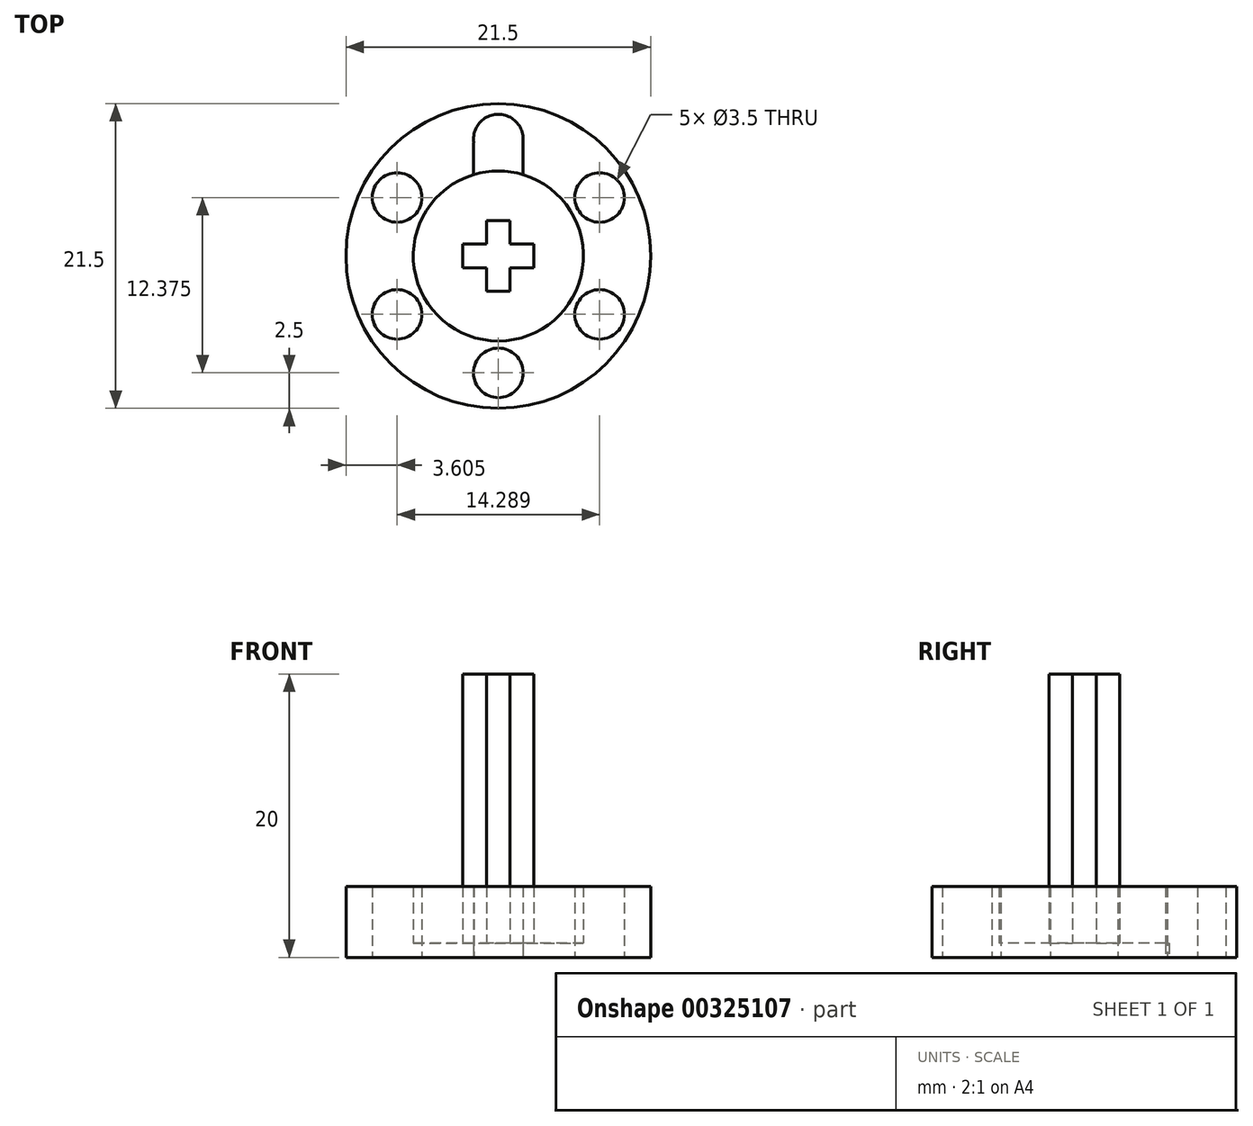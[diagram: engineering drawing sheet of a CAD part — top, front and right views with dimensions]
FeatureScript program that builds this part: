
annotation { "Feature Type Name" : "Feature", "Feature Type Description" : "" }
export const myFeature = defineFeature(function(context is Context, id is Id, definition is map)
    precondition{}
    {
        {
            var Q0;
            Q0=qCreatedBy(makeId("Top.planeOp"),FACE);
            var sketch = newSketch(context, id + "F0", { "sketchPlane" : qUnion([Q0])});
            skLineSegment(sketch, "E0", {"start": v(-0.83, 2.5) * mm, "end": v(0.83, 2.5) * mm});
            skLineSegment(sketch, "E1", {"start": v(0.83, -2.5) * mm, "end": v(-0.83, -2.5) * mm});
            skLineSegment(sketch, "E2.left", {"start": v(-2.5, 0.83) * mm, "end": v(-2.5, -0.83) * mm});
            skLineSegment(sketch, "E2.right", {"start": v(2.5, 0.83) * mm, "end": v(2.5, -0.83) * mm});
            skPoint(sketch, "E3", {"position": v(-0.83, 0.83) * mm});
            skPoint(sketch, "E4", {"position": v(0.83, 0.83) * mm});
            skPoint(sketch, "E5", {"position": v(0.83, -0.83) * mm});
            skPoint(sketch, "E6", {"position": v(-0.83, -0.83) * mm});
            skLineSegment(sketch, "E7", {"start": v(-0.83, -2.5) * mm, "end": v(-0.83, -0.83) * mm});
            skLineSegment(sketch, "E8", {"start": v(-0.83, -0.83) * mm, "end": v(-0.83, 0.83) * mm});
            skLineSegment(sketch, "E9", {"start": v(-0.83, 0.83) * mm, "end": v(-0.83, 2.5) * mm});
            skLineSegment(sketch, "E10", {"start": v(-2.5, -0.83) * mm, "end": v(-0.83, -0.83) * mm});
            skLineSegment(sketch, "E11", {"start": v(0.83, -0.83) * mm, "end": v(2.5, -0.83) * mm});
            skLineSegment(sketch, "E12", {"start": v(-0.83, -0.83) * mm, "end": v(0.83, -0.83) * mm});
            skLineSegment(sketch, "E13", {"start": v(-2.5, 0.83) * mm, "end": v(-0.83, 0.83) * mm});
            skLineSegment(sketch, "E14", {"start": v(-0.83, 0.83) * mm, "end": v(0.83, 0.83) * mm});
            skLineSegment(sketch, "E15", {"start": v(2.5, 0.83) * mm, "end": v(0.83, 0.83) * mm});
            skLineSegment(sketch, "E16", {"start": v(0.83, 2.5) * mm, "end": v(0.83, 0.83) * mm});
            skLineSegment(sketch, "E17", {"start": v(0.83, -0.83) * mm, "end": v(0.83, 0.83) * mm});
            skLineSegment(sketch, "E18", {"start": v(0.83, -2.5) * mm, "end": v(0.83, -0.83) * mm});
            skPoint(sketch, "E19", {"position": v(0, 0) * mm});
            skLineSegment(sketch, "E20", {"start": v(-0.83, -0.83) * mm, "end": v(0.83, 0.83) * mm, "construction": true});
            skLineSegment(sketch, "E21", {"start": v(-0.83, 0.83) * mm, "end": v(0.83, -0.83) * mm, "construction": true});
            skSolve(sketch);
        }
        {
            var Q0;
            Q0=qCreatedBy(makeId("Top.planeOp"),FACE);
            var sketch = newSketch(context, id + "F1", { "sketchPlane" : qUnion([Q0])});
            skCircle(sketch, "E22", {"center": v(0, 0) * mm, "radius": 6 * mm});
            skLineSegment(sketch, "E23", {"start": v(-1.75, 5.74) * mm, "end": v(-1.75, 8) * mm});
            skLineSegment(sketch, "E24", {"start": v(-1.75, 8) * mm, "end": v(1.75, 8) * mm});
            skLineSegment(sketch, "E25", {"start": v(1.75, 8) * mm, "end": v(1.75, 5.74) * mm});
            skPoint(sketch, "E26", {"position": v(0, 8) * mm});
            skCircle(sketch, "E27", {"center": v(0, 0) * mm, "radius": 10.75 * mm});
            skCircle(sketch, "E28", {"center": v(0, 0) * mm, "radius": 10 * mm});
            skCircle(sketch, "E29", {"center": v(0, -8.25) * mm, "radius": 1.75 * mm});
            skPoint(sketch, "E30", {"position": v(0, -10) * mm});
            skCircle(sketch, "E31.1.0", {"center": v(7.14, -4.13) * mm, "radius": 1.75 * mm});
            skCircle(sketch, "E31.2.0", {"center": v(7.14, 4.12) * mm, "radius": 1.75 * mm});
            skCircle(sketch, "E31.3.0", {"center": v(0, 8.25) * mm, "radius": 1.75 * mm});
            skCircle(sketch, "E31.4.0", {"center": v(-7.14, 4.13) * mm, "radius": 1.75 * mm});
            skCircle(sketch, "E31.5.0", {"center": v(-7.14, -4.13) * mm, "radius": 1.75 * mm});
            skSolve(sketch);
        }
        {
            var Q0;
            Q0=makeQuery(id+"F0.imprint","IMPRINT",FACE,{"disambiguationData":[TD([[makeQuery(id+"F0.imprint","IMPRINT",EDGE,{"derivedFrom":sQuery(id+"F0.wireOp",EDGE,"E0")}),-1.0]])]});
            var Q1;
            Q1=makeQuery(id+"F0.imprint","IMPRINT",FACE,{"disambiguationData":[TD([[makeQuery(id+"F0.imprint","IMPRINT",EDGE,{"derivedFrom":sQuery(id+"F0.wireOp",EDGE,"E2.left")}),1.0]])]});
            var Q2;
            Q2=makeQuery(id+"F0.imprint","IMPRINT",FACE,{"disambiguationData":[TD([[makeQuery(id+"F0.imprint","IMPRINT",EDGE,{"derivedFrom":sQuery(id+"F0.wireOp",EDGE,"E1")}),-1.0]])]});
            var Q3;
            Q3=makeQuery(id+"F0.imprint","IMPRINT",FACE,{"disambiguationData":[TD([[makeQuery(id+"F0.imprint","IMPRINT",EDGE,{"derivedFrom":sQuery(id+"F0.wireOp",EDGE,"E8")}),-1.0]])]});
            var Q4;
            Q4=makeQuery(id+"F0.imprint","IMPRINT",FACE,{"disambiguationData":[TD([[makeQuery(id+"F0.imprint","IMPRINT",EDGE,{"derivedFrom":sQuery(id+"F0.wireOp",EDGE,"E2.right")}),-1.0]])]});
            extrude(context, id + "F2", {"entities" : qUnion([Q0, Q1, Q2, Q3, Q4]), "depth" : 20 * mm});
        }
        {
            var Q0;
            {var subQ14=sQuery(id+"F1.wireOp",EDGE,"E23");Q0=makeQuery(id+"F1.imprint","IMPRINT",FACE,{"disambiguationData":[TD([[makeQuery(id+"F1.imprint","IMPRINT",EDGE,{"derivedFrom":subQ14}),1.0]])]});}
            var Q1;
            Q1=makeQuery(id+"F1.imprint","IMPRINT",FACE,{"disambiguationData":[TD([[makeQuery(id+"F1.imprint","IMPRINT",EDGE,{"derivedFrom":sQuery(id+"F1.wireOp",EDGE,"E27")}),1.0]])]});
            extrude(context, id + "F3", {"entities" : qUnion([Q0, Q1]), "depth" : 5 * mm});
        }
        {
            var Q0;
            {var subQ0=sQuery(id+"F1.wireOp",EDGE,"E22");var subQ1=makeQuery(id+"F1.imprint","INTERSECT",VERTEX,{"derivedFrom":[subQ0,sQuery(id+"F1.wireOp",EDGE,"E23")]});Q0=makeQuery(id+"F1.imprint","IMPRINT",FACE,{"disambiguationData":[TD([[makeQuery(id+"F1.imprint","IMPRINT",EDGE,{"disambiguationData":[TD([[subQ1,1.0]])],"derivedFrom":subQ0}),1.0]])]});}
            extrude(context, id + "F4", {"entities" : qUnion([Q0]), "operationType" : NewBodyOperationType.ADD, "depth" : 1 * mm});
        }
    });
